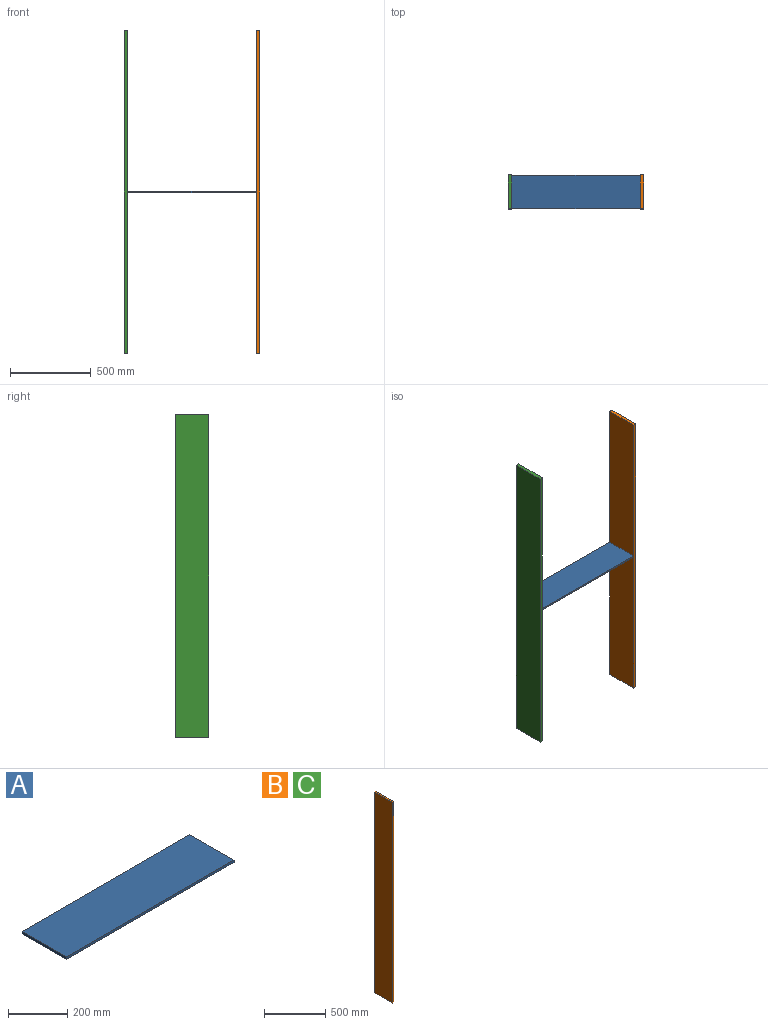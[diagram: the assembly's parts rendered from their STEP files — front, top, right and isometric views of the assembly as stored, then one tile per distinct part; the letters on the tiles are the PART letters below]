
ASSEMBLY  parts=3 mates=6
PART A: 6 faces, bbox 800x210x10 mm
  f0: plane 800x10mm, normal (0,1,0), area 8000mm2, adj f1,f3,f4,f5
  f1: plane 210x10mm, normal (-1,0,0), area 2100mm2, adj f0,f2,f4,f5
  f2: plane 800x10mm, normal (0,-1,0), area 8000mm2, adj f1,f3,f4,f5
  f3: plane 210x10mm, normal (1,0,0), area 2100mm2, adj f0,f2,f4,f5
  f4: plane 800x210mm, normal (0,0,1), area 168000mm2, adj f0,f1,f2,f3
  f5: plane 800x210mm, normal (0,0,-1), area 168000mm2, adj f0,f1,f2,f3
PART B: 6 faces, bbox 20x210x2000 mm
  f0: plane 2000x210mm, normal (-1,0,0), area 420000mm2, adj f1,f3,f4,f5
  f1: plane 2000x20mm, normal (0,-1,0), area 40000mm2, adj f0,f2,f4,f5
  f2: plane 2000x210mm, normal (1,0,0), area 420000mm2, adj f1,f3,f4,f5
  f3: plane 2000x20mm, normal (0,1,0), area 40000mm2, adj f0,f2,f4,f5
  f4: plane 210x20mm, normal (0,0,1), area 4200mm2, adj f0,f1,f2,f3
  f5: plane 210x20mm, normal (0,0,-1), area 4200mm2, adj f0,f1,f2,f3
PART C: same geometry as B
PLACE A t=(-651.79,-248.35,666.73)mm
PLACE B t=(-11.15,-238.56,-328.27)mm
PLACE C t=(-831.15,-238.56,-328.27)mm
MATE fastened A.f1 <-> C.f2  axis (-1,0,0) through (-884.2,-248.69,671.73)mm
MATE parallel A.f4 <-> C.f4  axis (0,0,1) through (-484.2,-248.69,676.73)mm
MATE planar A.f2 <-> B.f1  axis (0,-1,0) through (-484.2,-353.69,671.73)mm
MATE planar B.f4 <-> C.f4  axis (0,0,1) through (-74.2,-353.69,1671.73)mm
MATE planar C.f1 <-> B.f1  axis (0,-1,0) through (-894.2,-353.69,671.73)mm
MATE fastened A.f3 <-> B.f0  axis (1,0,0) through (-84.2,-248.69,671.73)mm
